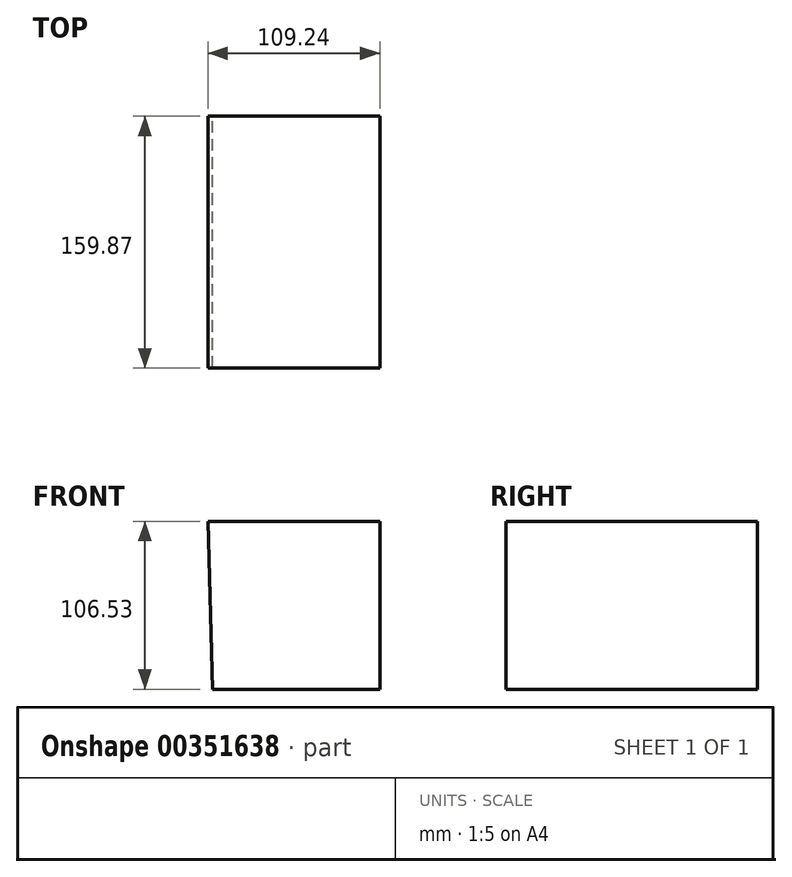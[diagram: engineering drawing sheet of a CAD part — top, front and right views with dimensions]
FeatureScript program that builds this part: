
annotation { "Feature Type Name" : "Feature", "Feature Type Description" : "" }
export const myFeature = defineFeature(function(context is Context, id is Id, definition is map)
    precondition{}
    {
        {
            var Q0;
            Q0=qCreatedBy(makeId("Front.planeOp"),FACE);
            var sketch = newSketch(context, id + "F0", { "sketchPlane" : qUnion([Q0])});
            skLineSegment(sketch, "E0", {"start": v(-57.69, 51.22) * mm, "end": v(51.55, 51.22) * mm});
            skLineSegment(sketch, "E1", {"start": v(51.55, 51.22) * mm, "end": v(51.55, -55.3) * mm});
            skLineSegment(sketch, "E2", {"start": v(51.55, -55.3) * mm, "end": v(-54.77, -55.3) * mm});
            skLineSegment(sketch, "E3", {"start": v(-54.77, -55.3) * mm, "end": v(-57.69, 51.22) * mm});
            skSolve(sketch);
        }
        {
            var Q0;
            Q0 = qSketchRegion(id + "F0", true);
            extrude(context, id + "F1", {"entities" : qUnion([Q0]), "depth" : 159.87 * mm});
        }
    });
